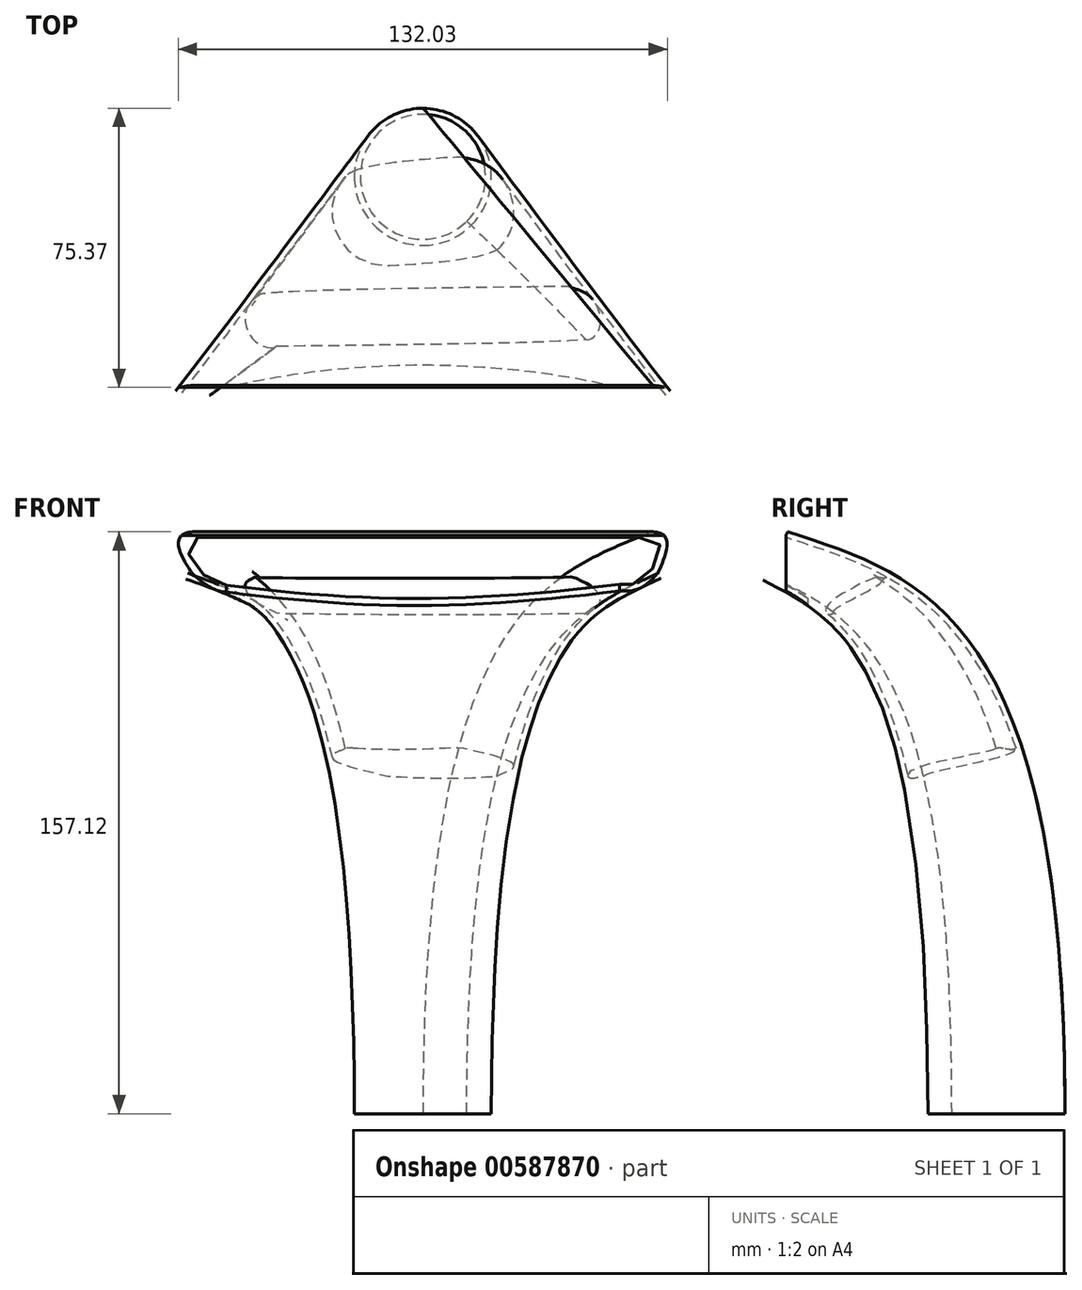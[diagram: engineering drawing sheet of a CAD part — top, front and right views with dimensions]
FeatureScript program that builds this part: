
annotation { "Feature Type Name" : "Feature", "Feature Type Description" : "" }
export const myFeature = defineFeature(function(context is Context, id is Id, definition is map)
    precondition{}
    {
        {
            var Q0;
            Q0=qCreatedBy(makeId("Top.planeOp"),FACE);
            var sketch = newSketch(context, id + "F0", { "sketchPlane" : qUnion([Q0])});
            skCircle(sketch, "E0", {"center": v(0, 0) * mm, "radius": 18.5 * mm});
            skSolve(sketch);
        }
        {
            var Q0;
            Q0=qCreatedBy(makeId("Right.planeOp"),FACE);
            var sketch = newSketch(context, id + "F1", { "sketchPlane" : qUnion([Q0])});
            skLineSegment(sketch, "E1", {"start": v(0, 0) * mm, "end": v(0, 150) * mm, "construction": true});
            skLineSegment(sketch, "E2", {"start": v(0, 150) * mm, "end": v(-60, 150) * mm, "construction": true});
            skFitSpline(sketch, "E3", {"points": [v(0, 0) * mm, v(0, 75) * mm, v(-15.54, 122.68) * mm, v(-60, 150) * mm], "startDerivative": vector(8.64, 204.46) * mm, "endDerivative": vector(-147.3, 75.33) * mm});
            skSolve(sketch);
        }
        {
            var Q0;
            Q0=sQuery(id+"F1.wireOp",VERTEX,"E3.end");
            var Q1;
            Q1=sQuery(id+"F1.wireOp",EDGE,"E3");
            cPlane(context, id + "F2", {"entities" : qUnion([Q0, Q1]), "cplaneType" : CPlaneType.CURVE_POINT, "offset" : 25 * mm, "width" : 150 * mm, "height" : 150 * mm});
        }
        {
            var Q0;
            Q0=qCreatedBy(id+"F2.planeOp",FACE);
            var sketch = newSketch(context, id + "F3", { "sketchPlane" : qUnion([Q0])});
            skLineSegment(sketch, "E4.bottom", {"start": v(62.09, 99.6) * mm, "end": v(-62.09, 99.6) * mm});
            skLineSegment(sketch, "E4.top", {"start": v(62.09, 114.22) * mm, "end": v(-62.09, 114.22) * mm});
            skLineSegment(sketch, "E4.left", {"start": v(67.09, 104.6) * mm, "end": v(67.09, 109.22) * mm});
            skLineSegment(sketch, "E4.right", {"start": v(-67.09, 104.6) * mm, "end": v(-67.09, 109.22) * mm});
            skPoint(sketch, "E4.middle", {"position": v(0, 106.9) * mm});
            skPoint(sketch, "E5.visualSharp", {"position": v(-67.09, 114.22) * mm});
            skArc(sketch, "E5.filletArc", {"start": v(-62.09, 114.22) * mm, "mid": v(-65.62, 112.76) * mm, "end": v(-67.09, 109.22) * mm});
            skPoint(sketch, "E6.visualSharp", {"position": v(-67.09, 99.6) * mm});
            skArc(sketch, "E6.filletArc", {"start": v(-67.09, 104.6) * mm, "mid": v(-65.62, 101.06) * mm, "end": v(-62.09, 99.6) * mm});
            skPoint(sketch, "E7.visualSharp", {"position": v(67.09, 99.6) * mm});
            skArc(sketch, "E7.filletArc", {"start": v(62.09, 99.6) * mm, "mid": v(65.62, 101.06) * mm, "end": v(67.09, 104.6) * mm});
            skPoint(sketch, "E8.visualSharp", {"position": v(67.09, 114.22) * mm});
            skArc(sketch, "E8.filletArc", {"start": v(67.09, 109.22) * mm, "mid": v(65.62, 112.76) * mm, "end": v(62.09, 114.22) * mm});
            skPoint(sketch, "E9.visualSharp", {"position": v(-65.59, 112.72) * mm});
            skPoint(sketch, "E10.visualSharp", {"position": v(-65.59, 101.1) * mm});
            skPoint(sketch, "E11.visualSharp", {"position": v(65.59, 112.72) * mm});
            skPoint(sketch, "E12.visualSharp", {"position": v(65.59, 101.1) * mm});
            skSolve(sketch);
        }
        {
            var Q0;
            Q0=makeQuery(id+"F0.imprint","IMPRINT",FACE,{"disambiguationData":[TD([[makeQuery(id+"F0.imprint","IMPRINT",EDGE,{"derivedFrom":sQuery(id+"F0.wireOp",EDGE,"E0")}),1.0]])]});
            var Q1;
            Q1=makeQuery(id+"F3.imprint","IMPRINT",FACE,{"disambiguationData":[TD([[makeQuery(id+"F3.imprint","IMPRINT",EDGE,{"derivedFrom":sQuery(id+"F3.wireOp",EDGE,"E4.bottom")}),-1.0]])]});
            var Q2;
            Q2 = qConstructionFilter(qBodyType(qCreatedBy(id + "F1" ,EDGE), BodyType.WIRE), ConstructionObject.NO);
            var Q3;
            Q3=sQuery(id+"F1.wireOp",VERTEX,"E3.2.internal");
            var Q4;
            Q4=sQuery(id+"F1.wireOp",VERTEX,"E3.1.internal");
            loft(context, id + "F4", {"startCondition" : LoftEndDerivativeType.NORMAL_TO_PROFILE, "startMagnitude" : 2.5, "sheetProfilesArray" : [{ "sheetProfileEntities" : qUnion([Q0]) }, { "sheetProfileEntities" : qUnion([Q1]) }], "guidesArray" : [{ "guideEntities" : qUnion([Q2]), "guideDerivativeType" : LoftGuideDerivativeType.DEFAULT, "guideDerivativeMagnitude" : 1 }], "connections" : [{ "connectionEntities" : qUnion([Q3, Q4]), "connectionEdgeQueries" : qUnion([]), "connectionEdgeParameters" : [] }]});
        }
        {
            var Q0;
            Q0=makeQuery(id+"F4.opLoft","CAP_FACE",FACE,{"disambiguationData":[OSD([makeQuery(id+"F0.imprint","IMPRINT",FACE,{"disambiguationData":[TD([[makeQuery(id+"F0.imprint","IMPRINT",EDGE,{"derivedFrom":sQuery(id+"F0.wireOp",EDGE,"E0")}),1.0]])]})])],"isStart":true});
            var Q1;
            Q1=makeQuery(id+"F4.opLoft","CAP_FACE",FACE,{"disambiguationData":[OSD([makeQuery(id+"F3.imprint","IMPRINT",FACE,{"disambiguationData":[TD([[makeQuery(id+"F3.imprint","IMPRINT",EDGE,{"derivedFrom":sQuery(id+"F3.wireOp",EDGE,"E4.bottom")}),-1.0]])]})])],"isStart":true});
            shell(context, id + "F5", {"entities" : qUnion([Q0, Q1]), "thickness" : 1.6 * mm});
        }
        {
            var Q0;
            Q0=qCreatedBy(makeId("Top.planeOp"),FACE);
            var sketch = newSketch(context, id + "F6", { "sketchPlane" : qUnion([Q0])});
            skLineSegment(sketch, "E13", {"start": v(0, 0) * mm, "end": v(0, -72.7) * mm, "construction": true});
            skLineSegment(sketch, "E14.bottom", {"start": v(88.7, -56.87) * mm, "end": v(-88.7, -56.87) * mm});
            skLineSegment(sketch, "E14.top", {"start": v(88.7, -88.53) * mm, "end": v(-88.7, -88.53) * mm});
            skLineSegment(sketch, "E14.left", {"start": v(88.7, -56.87) * mm, "end": v(88.7, -88.53) * mm});
            skLineSegment(sketch, "E14.right", {"start": v(-88.7, -56.87) * mm, "end": v(-88.7, -88.53) * mm});
            skPoint(sketch, "E14.middle", {"position": v(0, -72.7) * mm});
            skSolve(sketch);
        }
        {
            var Q0;
            Q0=makeQuery(id+"F6.imprint","IMPRINT",FACE,{"disambiguationData":[TD([[makeQuery(id+"F6.imprint","IMPRINT",EDGE,{"derivedFrom":sQuery(id+"F6.wireOp",EDGE,"E14.bottom")}),1.0]])]});
            extrude(context, id + "F7", {"entities" : qUnion([Q0]), "operationType" : NewBodyOperationType.REMOVE, "depth" : 214 * mm, "offsetDistance" : 25 * mm});
        }
        {
            var Q0;
            Q0=qCreatedBy(makeId("Top.planeOp"),FACE);
            var sketch = newSketch(context, id + "F8", { "sketchPlane" : qUnion([Q0])});
            skLineSegment(sketch, "E15", {"start": v(0, 0) * mm, "end": v(0, -290.23) * mm, "construction": true});
            skCircle(sketch, "E16", {"center": v(0, -290.23) * mm, "radius": 239.33 * mm});
            skSolve(sketch);
        }
        {
            var Q0;
            Q0=makeQuery(id+"F8.imprint","IMPRINT",FACE,{"disambiguationData":[TD([[makeQuery(id+"F8.imprint","IMPRINT",EDGE,{"derivedFrom":sQuery(id+"F8.wireOp",EDGE,"E16")}),1.0]])]});
            extrude(context, id + "F9", {"entities" : qUnion([Q0]), "operationType" : NewBodyOperationType.REMOVE, "depth" : 147.7 * mm, "offsetDistance" : 25 * mm});
        }
    });
